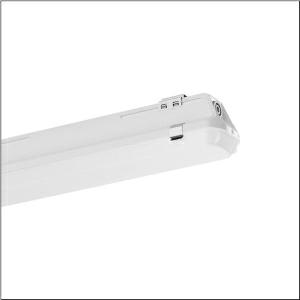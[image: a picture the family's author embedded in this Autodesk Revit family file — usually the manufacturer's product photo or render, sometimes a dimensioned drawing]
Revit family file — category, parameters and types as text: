
# Revit family: monsun_r__11_emergency_51fp10dp468h2_0287
name_source: partatom
category: Lighting Fixtures
units: mm (PartAtom-declared; Revit-internal decimal feet)

## family parameters
Cut with Voids When Loaded = No
Host = Face
Light Source = No
Part Type = Normal
Room Calculation Point = No
Round Connector Dimension = Use Diameter
Shared = No

## types (1)
- --- (1 x LED, 890 lm, 6.9 W, 4000K)
    Apparent Load = 7 VA
    CIE Flux Codes = 47 77 93 94 100
    Color Rendering = 80
    Color Temperature = 4000K
    Default Elevation = 1800 mm
    Description = Monsun® 11 emergency, damp-proof luminaire, chain hanger, primary optical cover: enclosure, of PMMA, light emission: direct distribution, primary light characteristic: symmetric, installation type: suspended mounting, surface-mounted, horizontal mounting, vertical mounting, LED, rated luminous flux: 6.050lm, luminous efficacy: 175lm/W, light colour: 840, colour temperature: 4000K, control gear: ECG DALI, with terminal, 5-pole, max. 2.5mm², mains connection: 220..240V, AC/DC, 0/50..60Hz, rated input power: 35W, luminaire housing, of glass-fibre reinforced polyester, uncoated, bright grey, incl. chain hanger, length: 1.590mm, width: 90mm, height: 88mm, clip for enclosure, of stainless steel (V2A), ceiling mounting element, of stainless steel (V2A), chain hanger, of stainless steel (V2A), protection rating (complete): IP66, insulation class (complete): insulation class I (protective earthing), certification: CE, UKCA, protection symbol: D, impact resistance: IK04, permissible operating ambient temperature: -25..+40°C, standard: EN 60598-2-22, EN 50419, EN 60598-2-1, no direct snow, no direct sun, no direct rain, for indoor or canopied outdoor use, corresponds to IFS (International Featured Standards) requirements for safety and quality in the food industry, contact your sales advisor before using the luminaires in applications with unclear chemical exposure, large temperature fluctuations or condensation-forming humidity, LABS conformity tested according to VDMA 24364:2018-05, packaging unit: 1 piece
    Height = 89 mm
    Lamp = 1 x LED
    Lamp Light Flux = 890 lm
    Lamp Power = 6.9 W
    Lamp count = 1
    Length = 1590 mm
    Luminous efficacy = 129 lm/W
    Manufacturer = Siteco
    ModVariant = No
    Model = 51FP10DP468H2
    Mounting Place = Ceiling
    Mounting Type = Surface mounted
    Number of Poles = 1
    OnlyDefault = Yes
    Power Factor = 1
    Product Name = Monsun® 11 emergency
    Product group = damp-proof luminaire
    ProductGroupID = 301
    Protection Class = Protection class I
    Protection Degree = IP 66
    RLX_Detail_Level = 1
    RLX_Emergency_Light_Flux = 0 lm
    RLX_Emergency_Type = 0
    RLX_Emergency_Type_DB = No
    RlxData = <blob elided: 92513 chars, md5=a48e49ec>
    Socket = socket
    Standby Power = 0 W
    System Light Flux = 890 lm
    System Power = 7 W
    Type Comments = : equivalent power supply (DC)
    Type Image = l_1004748.jpg
    URL = http://relux.com
    VarID = @adj_152537
    Voltage = 0 V
    Weight = 0.00 kg
    Width = 90 mm

## geometry (parser evidence)
native form markers: Blend x4, Sweep x15
no freeform markers — native parametric forms only
